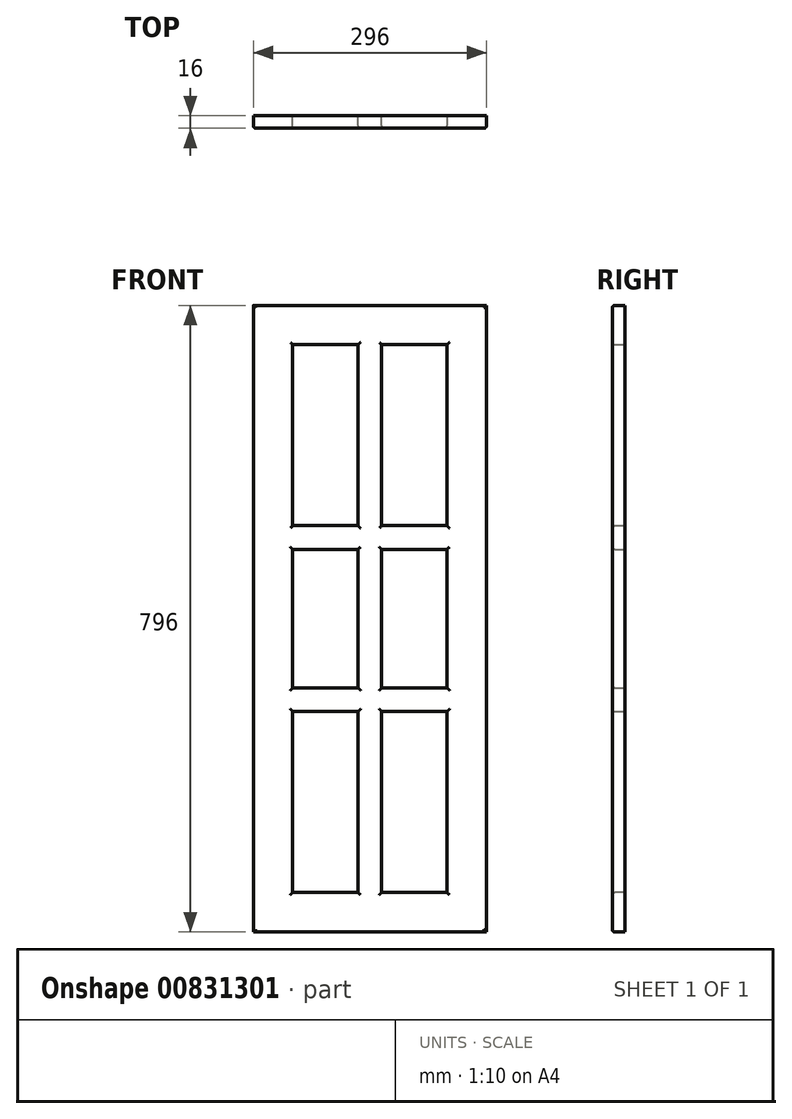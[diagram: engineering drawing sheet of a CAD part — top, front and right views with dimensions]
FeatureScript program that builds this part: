
annotation { "Feature Type Name" : "Feature", "Feature Type Description" : "" }
export const myFeature = defineFeature(function(context is Context, id is Id, definition is map)
    precondition{}
    {
        {
            var Q0;
            Q0=qCreatedBy(makeId("Front.planeOp"),FACE);
            var sketch = newSketch(context, id + "F0", { "sketchPlane" : qUnion([Q0])});
            skLineSegment(sketch, "E0.bottom", {"start": v(0, 0) * mm, "end": v(28.85, 0) * mm});
            skLineSegment(sketch, "E0.top", {"start": v(0, 37.88) * mm, "end": v(28.85, 37.88) * mm});
            skLineSegment(sketch, "E0.left", {"start": v(0, 0) * mm, "end": v(0, 37.88) * mm});
            skLineSegment(sketch, "E0.right", {"start": v(28.85, 0) * mm, "end": v(28.85, 37.88) * mm});
            skSolve(sketch);
        }
        {
            var Q0;
            Q0=makeQuery(id+"F0.imprint","IMPRINT",FACE,{"disambiguationData":[TD([[makeQuery(id+"F0.imprint","IMPRINT",EDGE,{"derivedFrom":sQuery(id+"F0.wireOp",EDGE,"E0.bottom")}),1.0]])]});
            extrude(context, id + "F1", {"entities" : qUnion([Q0]), "depth" : 16 * mm, "offsetDistance" : 25.4 * mm});
        }
        {
            var Q0;
            Q0=makeQuery(id+"F1.opExtrude","SWEPT_FACE",FACE,{"disambiguationData":[OSD([sQuery(id+"F0.wireOp",EDGE,"E0.left")])]});
            extrude(context, id + "F2", {"entities" : qUnion([Q0]), "operationType" : NewBodyOperationType.ADD, "oppositeDirection" : true, "depth" : 296 * mm, "offsetDistance" : 25.4 * mm});
        }
        {
            var Q0;
            {var subQ0=sQuery(id+"F0.wireOp",EDGE,"E0.bottom");Q0=makeQuery(id+"F2.boolean.opBoolean","MERGE",FACE,{"derivedFrom":[makeQuery(id+"F1.opExtrude","SWEPT_FACE",FACE,{"disambiguationData":[OSD([subQ0])]}),makeQuery(id+"F2.opExtrude","SWEPT_FACE",FACE,{"disambiguationData":[OSD([subQ0,sQuery(id+"F0.wireOp",EDGE,"E0.left")])]})]});}
            extrude(context, id + "F3", {"entities" : qUnion([Q0]), "operationType" : NewBodyOperationType.ADD, "oppositeDirection" : true, "depth" : 996 * mm, "offsetDistance" : 25 * mm});
        }
        {
            var Q0;
            {var subQ0=sQuery(id+"F0.wireOp",EDGE,"E0.left");var subQ1=sQuery(id+"F0.wireOp",EDGE,"E0.bottom");Q0=makeQuery(id+"F3.boolean.opBoolean","MERGE",FACE,{"derivedFrom":[makeQuery(id+"F2.boolean.opBoolean","MERGE",FACE,{"derivedFrom":[makeQuery(id+"F1.opExtrude","CAP_FACE",FACE,{"disambiguationData":[OSD([subQ1,sQuery(id+"F0.wireOp",EDGE,"E0.top"),subQ0,sQuery(id+"F0.wireOp",EDGE,"E0.right")])],"isStart":false}),makeQuery(id+"F2.opExtrude","SWEPT_FACE",FACE,{"disambiguationData":[OSD([subQ0]),TDD([makeQuery(id+"F1.opExtrude","CAP_EDGE",EDGE,{"disambiguationData":[OSD([subQ0])],"isStart":false})])]})]}),makeQuery(id+"F3.opExtrude","SWEPT_FACE",FACE,{"disambiguationData":[OSD([subQ1,subQ0]),TDD([makeQuery(id+"F2.boolean.opBoolean","MERGE",EDGE,{"derivedFrom":[makeQuery(id+"F1.opExtrude","CAP_EDGE",EDGE,{"disambiguationData":[OSD([subQ1])],"isStart":false}),makeQuery(id+"F2.opExtrude","SWEPT_EDGE",EDGE,{"disambiguationData":[OSD([subQ1,subQ0]),TDD([makeQuery(id+"F1.opExtrude","CAP_VERTEX",VERTEX,{"disambiguationData":[OSD([subQ1,subQ0])],"isStart":false})])]})]})])]})]});}
            var sketch = newSketch(context, id + "F4", { "sketchPlane" : qUnion([Q0])});
            skLineSegment(sketch, "E1.bottom", {"start": v(48.4, 906.79) * mm, "end": v(248.24, 906.79) * mm});
            skLineSegment(sketch, "E1.top", {"start": v(48.4, 105.66) * mm, "end": v(248.24, 105.66) * mm});
            skLineSegment(sketch, "E1.left", {"start": v(48.4, 906.79) * mm, "end": v(48.4, 105.66) * mm});
            skLineSegment(sketch, "E1.right", {"start": v(248.24, 906.79) * mm, "end": v(248.24, 105.66) * mm});
            skSolve(sketch);
        }
        {
            var Q0;
            Q0=makeQuery(id+"F4.imprint","IMPRINT",FACE,{"disambiguationData":[TD([[makeQuery(id+"F4.imprint","IMPRINT",EDGE,{"derivedFrom":sQuery(id+"F4.wireOp",EDGE,"E1.bottom")}),-1.0]])]});
            extrude(context, id + "F5", {"entities" : qUnion([Q0]), "operationType" : NewBodyOperationType.REMOVE, "oppositeDirection" : true, "depth" : 5 * mm, "offsetDistance" : 25 * mm});
        }
        {
            var Q0;
            Q0=makeQuery(id+"F5.boolean.opBoolean","COPY",FACE,{"derivedFrom":makeQuery(id+"F5.opExtrude","SWEPT_FACE",FACE,{"disambiguationData":[OSD([sQuery(id+"F4.wireOp",EDGE,"E1.bottom")])]})});
            extrude(context, id + "F6", {"entities" : qUnion([Q0]), "operationType" : NewBodyOperationType.REMOVE, "oppositeDirection" : true, "depth" : 39.2 * mm, "offsetDistance" : 25 * mm});
        }
        {
            var Q0;
            {var subQ0=sQuery(id+"F4.wireOp",EDGE,"E1.right");Q0=makeQuery(id+"F6.boolean.opBoolean","MERGE",FACE,{"derivedFrom":[makeQuery(id+"F5.boolean.opBoolean","COPY",FACE,{"derivedFrom":makeQuery(id+"F5.opExtrude","SWEPT_FACE",FACE,{"disambiguationData":[OSD([subQ0])]})}),makeQuery(id+"F6.opExtrude","SWEPT_FACE",FACE,{"disambiguationData":[OSD([sQuery(id+"F4.wireOp",EDGE,"E1.bottom"),subQ0])]})]});}
            extrude(context, id + "F7", {"entities" : qUnion([Q0]), "operationType" : NewBodyOperationType.ADD, "depth" : 2.24 * mm, "offsetDistance" : 25 * mm});
        }
        {
            var Q0;
            Q0=makeQuery(id+"F5.boolean.opBoolean","COPY",FACE,{"derivedFrom":makeQuery(id+"F5.opExtrude","SWEPT_FACE",FACE,{"disambiguationData":[OSD([sQuery(id+"F4.wireOp",EDGE,"E1.top")])]})});
            extrude(context, id + "F8", {"entities" : qUnion([Q0]), "operationType" : NewBodyOperationType.REMOVE, "oppositeDirection" : true, "depth" : 55.66 * mm, "offsetDistance" : 25 * mm});
        }
        {
            var Q0;
            {var subQ0=sQuery(id+"F4.wireOp",EDGE,"E1.left");Q0=makeQuery(id+"F8.boolean.opBoolean","MERGE",FACE,{"derivedFrom":[makeQuery(id+"F6.boolean.opBoolean","MERGE",FACE,{"derivedFrom":[makeQuery(id+"F5.boolean.opBoolean","COPY",FACE,{"derivedFrom":makeQuery(id+"F5.opExtrude","SWEPT_FACE",FACE,{"disambiguationData":[OSD([subQ0])]})}),makeQuery(id+"F6.opExtrude","SWEPT_FACE",FACE,{"disambiguationData":[OSD([sQuery(id+"F4.wireOp",EDGE,"E1.bottom"),subQ0])]})]}),makeQuery(id+"F8.opExtrude","SWEPT_FACE",FACE,{"disambiguationData":[OSD([sQuery(id+"F4.wireOp",EDGE,"E1.top"),subQ0])]})]});}
            extrude(context, id + "F9", {"entities" : qUnion([Q0]), "operationType" : NewBodyOperationType.ADD, "depth" : 1.59 * mm, "offsetDistance" : 25 * mm});
        }
        {
            var Q0;
            {var subQ0=sQuery(id+"F4.wireOp",EDGE,"E1.top");var subQ1=sQuery(id+"F4.wireOp",EDGE,"E1.bottom");Q0=makeQuery(id+"F8.boolean.opBoolean","MERGE",FACE,{"derivedFrom":[makeQuery(id+"F6.boolean.opBoolean","MERGE",FACE,{"derivedFrom":[makeQuery(id+"F5.boolean.opBoolean","COPY",FACE,{"derivedFrom":makeQuery(id+"F5.opExtrude","CAP_FACE",FACE,{"disambiguationData":[OSD([subQ1,subQ0,sQuery(id+"F4.wireOp",EDGE,"E1.left"),sQuery(id+"F4.wireOp",EDGE,"E1.right")])],"isStart":false})}),makeQuery(id+"F6.opExtrude","SWEPT_FACE",FACE,{"disambiguationData":[OSD([subQ1]),TDD([makeQuery(id+"F5.boolean.opBoolean","COPY",EDGE,{"derivedFrom":makeQuery(id+"F5.opExtrude","CAP_EDGE",EDGE,{"disambiguationData":[OSD([subQ1])],"isStart":false})})])]})]}),makeQuery(id+"F8.opExtrude","SWEPT_FACE",FACE,{"disambiguationData":[OSD([subQ0]),TDD([makeQuery(id+"F5.boolean.opBoolean","COPY",EDGE,{"derivedFrom":makeQuery(id+"F5.opExtrude","CAP_EDGE",EDGE,{"disambiguationData":[OSD([subQ0])],"isStart":false})})])]})]});}
            var sketch = newSketch(context, id + "F10", { "sketchPlane" : qUnion([Q0])});
            skLineSegment(sketch, "E2.bottom", {"start": v(127.14, 946) * mm, "end": v(181.91, 946) * mm});
            skLineSegment(sketch, "E2.top", {"start": v(127.14, 50) * mm, "end": v(181.91, 50) * mm});
            skLineSegment(sketch, "E2.left", {"start": v(127.14, 946) * mm, "end": v(127.14, 50) * mm});
            skLineSegment(sketch, "E2.right", {"start": v(181.91, 946) * mm, "end": v(181.91, 50) * mm});
            skSolve(sketch);
        }
        {
            var Q0;
            Q0=makeQuery(id+"F10.imprint","IMPRINT",FACE,{"disambiguationData":[TD([[makeQuery(id+"F10.imprint","IMPRINT",EDGE,{"derivedFrom":sQuery(id+"F10.wireOp",EDGE,"E2.bottom")}),-1.0]])]});
            extrude(context, id + "F11", {"entities" : qUnion([Q0]), "operationType" : NewBodyOperationType.ADD, "depth" : 5 * mm, "offsetDistance" : 25 * mm});
        }
        {
            var Q0;
            Q0=makeQuery(id+"F11.opExtrude","SWEPT_FACE",FACE,{"disambiguationData":[OSD([sQuery(id+"F10.wireOp",EDGE,"E2.left")])]});
            extrude(context, id + "F12", {"entities" : qUnion([Q0]), "operationType" : NewBodyOperationType.REMOVE, "oppositeDirection" : true, "depth" : 5.86 * mm, "offsetDistance" : 25 * mm});
        }
        {
            var Q0;
            Q0=makeQuery(id+"F11.opExtrude","SWEPT_FACE",FACE,{"disambiguationData":[OSD([sQuery(id+"F10.wireOp",EDGE,"E2.right")])]});
            extrude(context, id + "F13", {"entities" : qUnion([Q0]), "operationType" : NewBodyOperationType.REMOVE, "oppositeDirection" : true, "depth" : 18.91 * mm, "offsetDistance" : 25 * mm});
        }
        {
            var Q0;
            {var subQ0=sQuery(id+"F10.wireOp",EDGE,"E2.left");var subQ1=sQuery(id+"F4.wireOp",EDGE,"E1.bottom");var subQ2=sQuery(id+"F4.wireOp",EDGE,"E1.top");var subQ3=sQuery(id+"F4.wireOp",EDGE,"E1.left");Q0=makeQuery(id+"F12.boolean.opBoolean","MERGE",FACE,{"derivedFrom":[makeQuery(id+"F11.boolean.opBoolean","SPLIT",FACE,{"disambiguationData":[TD([makeQuery(id+"F11.opExtrude","SWEPT_FACE",FACE,{"disambiguationData":[OSD([subQ0])]})])],"derivedFrom":makeQuery(id+"F8.boolean.opBoolean","MERGE",FACE,{"derivedFrom":[makeQuery(id+"F6.boolean.opBoolean","MERGE",FACE,{"derivedFrom":[makeQuery(id+"F5.boolean.opBoolean","COPY",FACE,{"derivedFrom":makeQuery(id+"F5.opExtrude","CAP_FACE",FACE,{"disambiguationData":[OSD([subQ1,subQ2,subQ3,sQuery(id+"F4.wireOp",EDGE,"E1.right")])],"isStart":false})}),makeQuery(id+"F6.opExtrude","SWEPT_FACE",FACE,{"disambiguationData":[OSD([subQ1]),TDD([makeQuery(id+"F5.boolean.opBoolean","COPY",EDGE,{"derivedFrom":makeQuery(id+"F5.opExtrude","CAP_EDGE",EDGE,{"disambiguationData":[OSD([subQ1])],"isStart":false})})])]})]}),makeQuery(id+"F8.opExtrude","SWEPT_FACE",FACE,{"disambiguationData":[OSD([subQ2]),TDD([makeQuery(id+"F5.boolean.opBoolean","COPY",EDGE,{"derivedFrom":makeQuery(id+"F5.opExtrude","CAP_EDGE",EDGE,{"disambiguationData":[OSD([subQ2])],"isStart":false})})])]})]})}),makeQuery(id+"F12.opExtrude","SWEPT_FACE",FACE,{"disambiguationData":[OSD([subQ0]),TDD([makeQuery(id+"F11.opExtrude","CAP_EDGE",EDGE,{"disambiguationData":[OSD([subQ0])],"isStart":true})])]})]});}
            var sketch = newSketch(context, id + "F14", { "sketchPlane" : qUnion([Q0])});
            skLineSegment(sketch, "E3.bottom", {"start": v(50, 870.78) * mm, "end": v(133, 870.78) * mm});
            skLineSegment(sketch, "E3.top", {"start": v(50, 835.83) * mm, "end": v(133, 835.83) * mm});
            skLineSegment(sketch, "E3.left", {"start": v(50, 870.78) * mm, "end": v(50, 835.83) * mm});
            skLineSegment(sketch, "E3.right", {"start": v(133, 870.78) * mm, "end": v(133, 835.83) * mm});
            skLineSegment(sketch, "E4.bottom", {"start": v(50, 539.3) * mm, "end": v(133, 539.3) * mm});
            skLineSegment(sketch, "E4.top", {"start": v(50, 484.02) * mm, "end": v(133, 484.02) * mm});
            skLineSegment(sketch, "E4.left", {"start": v(50, 539.3) * mm, "end": v(50, 484.02) * mm});
            skLineSegment(sketch, "E4.right", {"start": v(133, 539.3) * mm, "end": v(133, 484.02) * mm});
            skSolve(sketch);
        }
        {
            var Q0;
            {var subQ0=sQuery(id+"F10.wireOp",EDGE,"E2.right");var subQ1=sQuery(id+"F4.wireOp",EDGE,"E1.top");var subQ2=sQuery(id+"F4.wireOp",EDGE,"E1.right");var subQ3=sQuery(id+"F4.wireOp",EDGE,"E1.bottom");Q0=makeQuery(id+"F13.boolean.opBoolean","MERGE",FACE,{"derivedFrom":[makeQuery(id+"F11.boolean.opBoolean","SPLIT",FACE,{"disambiguationData":[TD([makeQuery(id+"F11.opExtrude","SWEPT_FACE",FACE,{"disambiguationData":[OSD([subQ0])]})])],"derivedFrom":makeQuery(id+"F8.boolean.opBoolean","MERGE",FACE,{"derivedFrom":[makeQuery(id+"F6.boolean.opBoolean","MERGE",FACE,{"derivedFrom":[makeQuery(id+"F5.boolean.opBoolean","COPY",FACE,{"derivedFrom":makeQuery(id+"F5.opExtrude","CAP_FACE",FACE,{"disambiguationData":[OSD([subQ3,subQ1,sQuery(id+"F4.wireOp",EDGE,"E1.left"),subQ2])],"isStart":false})}),makeQuery(id+"F6.opExtrude","SWEPT_FACE",FACE,{"disambiguationData":[OSD([subQ3]),TDD([makeQuery(id+"F5.boolean.opBoolean","COPY",EDGE,{"derivedFrom":makeQuery(id+"F5.opExtrude","CAP_EDGE",EDGE,{"disambiguationData":[OSD([subQ3])],"isStart":false})})])]})]}),makeQuery(id+"F8.opExtrude","SWEPT_FACE",FACE,{"disambiguationData":[OSD([subQ1]),TDD([makeQuery(id+"F5.boolean.opBoolean","COPY",EDGE,{"derivedFrom":makeQuery(id+"F5.opExtrude","CAP_EDGE",EDGE,{"disambiguationData":[OSD([subQ1])],"isStart":false})})])]})]})}),makeQuery(id+"F13.opExtrude","SWEPT_FACE",FACE,{"disambiguationData":[OSD([subQ0]),TDD([makeQuery(id+"F11.opExtrude","CAP_EDGE",EDGE,{"disambiguationData":[OSD([subQ0])],"isStart":true})])]})]});}
            var sketch = newSketch(context, id + "F15", { "sketchPlane" : qUnion([Q0])});
            skLineSegment(sketch, "E5.bottom", {"start": v(163, 876.14) * mm, "end": v(246, 876.14) * mm});
            skLineSegment(sketch, "E5.top", {"start": v(163, 831.26) * mm, "end": v(246, 831.26) * mm});
            skLineSegment(sketch, "E5.left", {"start": v(163, 876.14) * mm, "end": v(163, 831.26) * mm});
            skLineSegment(sketch, "E5.right", {"start": v(246, 876.14) * mm, "end": v(246, 831.26) * mm});
            skLineSegment(sketch, "E6.bottom", {"start": v(163, 602.8) * mm, "end": v(246, 602.8) * mm});
            skLineSegment(sketch, "E6.top", {"start": v(163, 550.28) * mm, "end": v(246, 550.28) * mm});
            skLineSegment(sketch, "E6.left", {"start": v(163, 602.8) * mm, "end": v(163, 550.28) * mm});
            skLineSegment(sketch, "E6.right", {"start": v(246, 602.8) * mm, "end": v(246, 550.28) * mm});
            skSolve(sketch);
        }
        {
            var Q0;
            Q0=makeQuery(id+"F14.imprint","IMPRINT",FACE,{"disambiguationData":[TD([[makeQuery(id+"F14.imprint","IMPRINT",EDGE,{"derivedFrom":sQuery(id+"F14.wireOp",EDGE,"E3.bottom")}),-1.0]])]});
            var Q1;
            Q1=makeQuery(id+"F15.imprint","IMPRINT",FACE,{"disambiguationData":[TD([[makeQuery(id+"F15.imprint","IMPRINT",EDGE,{"derivedFrom":sQuery(id+"F15.wireOp",EDGE,"E5.bottom")}),-1.0]])]});
            var Q2;
            Q2=makeQuery(id+"F15.imprint","IMPRINT",FACE,{"disambiguationData":[TD([[makeQuery(id+"F15.imprint","IMPRINT",EDGE,{"derivedFrom":sQuery(id+"F15.wireOp",EDGE,"E6.bottom")}),-1.0]])]});
            var Q3;
            Q3=makeQuery(id+"F14.imprint","IMPRINT",FACE,{"disambiguationData":[TD([[makeQuery(id+"F14.imprint","IMPRINT",EDGE,{"derivedFrom":sQuery(id+"F14.wireOp",EDGE,"E4.bottom")}),-1.0]])]});
            extrude(context, id + "F16", {"entities" : qUnion([Q0, Q1, Q2, Q3]), "operationType" : NewBodyOperationType.ADD, "depth" : 5 * mm, "offsetDistance" : 25 * mm});
        }
        {
            var Q0;
            Q0=makeQuery(id+"F16.opExtrude","SWEPT_FACE",FACE,{"disambiguationData":[OSD([sQuery(id+"F15.wireOp",EDGE,"E6.top")])]});
            var Q1;
            Q1=makeQuery(id+"F16.opExtrude","SWEPT_FACE",FACE,{"disambiguationData":[OSD([sQuery(id+"F14.wireOp",EDGE,"E4.top")])]});
            extrude(context, id + "F17", {"entities" : qUnion([Q0, Q1]), "operationType" : NewBodyOperationType.ADD, "depth" : 300 * mm, "offsetDistance" : 25 * mm});
        }
        {
            var Q0;
            Q0=makeQuery(id+"F16.opExtrude","SWEPT_FACE",FACE,{"disambiguationData":[OSD([sQuery(id+"F14.wireOp",EDGE,"E4.bottom")])]});
            var Q1;
            Q1=makeQuery(id+"F16.opExtrude","SWEPT_FACE",FACE,{"disambiguationData":[OSD([sQuery(id+"F15.wireOp",EDGE,"E6.bottom")])]});
            extrude(context, id + "F18", {"entities" : qUnion([Q0, Q1]), "operationType" : NewBodyOperationType.REMOVE, "oppositeDirection" : true, "depth" : 300 * mm, "offsetDistance" : 25 * mm});
        }
        {
            var Q0;
            Q0=makeQuery(id+"F16.opExtrude","SWEPT_FACE",FACE,{"disambiguationData":[OSD([sQuery(id+"F14.wireOp",EDGE,"E3.top")])]});
            extrude(context, id + "F19", {"entities" : qUnion([Q0]), "operationType" : NewBodyOperationType.ADD, "depth" : 324.8 * mm, "offsetDistance" : 25 * mm});
        }
        {
            var Q0;
            Q0=makeQuery(id+"F16.opExtrude","SWEPT_FACE",FACE,{"disambiguationData":[OSD([sQuery(id+"F14.wireOp",EDGE,"E3.bottom")])]});
            extrude(context, id + "F20", {"entities" : qUnion([Q0]), "operationType" : NewBodyOperationType.REMOVE, "oppositeDirection" : true, "depth" : 324.8 * mm, "offsetDistance" : 25 * mm});
        }
        {
            var Q0;
            Q0=makeQuery(id+"F18.boolean.opBoolean","COPY",FACE,{"derivedFrom":makeQuery(id+"F18.opExtrude","CAP_FACE",FACE,{"disambiguationData":[OSD([sQuery(id+"F14.wireOp",EDGE,"E4.bottom")])],"isStart":false})});
            extrude(context, id + "F21", {"entities" : qUnion([Q0]), "operationType" : NewBodyOperationType.ADD, "depth" : 250 * mm, "offsetDistance" : 25 * mm});
        }
        {
            var Q0;
            Q0=makeQuery(id+"F17.opExtrude","CAP_FACE",FACE,{"disambiguationData":[OSD([sQuery(id+"F14.wireOp",EDGE,"E4.top")])],"isStart":false});
            extrude(context, id + "F22", {"entities" : qUnion([Q0]), "operationType" : NewBodyOperationType.REMOVE, "oppositeDirection" : true, "depth" : 250 * mm, "offsetDistance" : 25 * mm});
        }
        {
            var Q0;
            Q0=makeQuery(id+"F20.boolean.opBoolean","COPY",FACE,{"derivedFrom":makeQuery(id+"F20.opExtrude","CAP_FACE",FACE,{"disambiguationData":[OSD([sQuery(id+"F14.wireOp",EDGE,"E3.bottom")])],"isStart":false})});
            extrude(context, id + "F23", {"entities" : qUnion([Q0]), "operationType" : NewBodyOperationType.ADD, "depth" : 100 * mm, "offsetDistance" : 25 * mm});
        }
        {
            var Q0;
            Q0=makeQuery(id+"F19.opExtrude","CAP_FACE",FACE,{"disambiguationData":[OSD([sQuery(id+"F14.wireOp",EDGE,"E3.top")])],"isStart":false});
            extrude(context, id + "F24", {"entities" : qUnion([Q0]), "operationType" : NewBodyOperationType.REMOVE, "oppositeDirection" : true, "depth" : 100 * mm, "offsetDistance" : 25 * mm});
        }
        {
            var Q0;
            Q0=makeQuery(id+"F23.opExtrude","CAP_FACE",FACE,{"disambiguationData":[OSD([sQuery(id+"F14.wireOp",EDGE,"E3.bottom")])],"isStart":false});
            extrude(context, id + "F25", {"entities" : qUnion([Q0]), "operationType" : NewBodyOperationType.ADD, "depth" : 50 * mm, "offsetDistance" : 25 * mm});
        }
        {
            var Q0;
            Q0=makeQuery(id+"F24.boolean.opBoolean","COPY",FACE,{"derivedFrom":makeQuery(id+"F24.opExtrude","CAP_FACE",FACE,{"disambiguationData":[OSD([sQuery(id+"F14.wireOp",EDGE,"E3.top")])],"isStart":false})});
            extrude(context, id + "F26", {"entities" : qUnion([Q0]), "operationType" : NewBodyOperationType.REMOVE, "oppositeDirection" : true, "depth" : 50 * mm, "offsetDistance" : 25 * mm});
        }
        {
            var Q0;
            Q0=makeQuery(id+"F22.boolean.opBoolean","COPY",FACE,{"derivedFrom":makeQuery(id+"F22.opExtrude","CAP_FACE",FACE,{"disambiguationData":[OSD([sQuery(id+"F14.wireOp",EDGE,"E4.top")])],"isStart":false})});
            extrude(context, id + "F27", {"entities" : qUnion([Q0]), "operationType" : NewBodyOperationType.ADD, "depth" : 134.02 * mm, "offsetDistance" : 25 * mm});
        }
        {
            var Q0;
            Q0=makeQuery(id+"F27.opExtrude","CAP_FACE",FACE,{"disambiguationData":[OSD([sQuery(id+"F14.wireOp",EDGE,"E4.top")])],"isStart":false});
            extrude(context, id + "F28", {"entities" : qUnion([Q0]), "operationType" : NewBodyOperationType.REMOVE, "oppositeDirection" : true, "depth" : 100 * mm, "offsetDistance" : 25 * mm});
        }
        {
            var Q0;
            Q0=makeQuery(id+"F26.boolean.opBoolean","COPY",FACE,{"derivedFrom":makeQuery(id+"F26.opExtrude","CAP_FACE",FACE,{"disambiguationData":[OSD([sQuery(id+"F14.wireOp",EDGE,"E3.top")])],"isStart":false})});
            extrude(context, id + "F29", {"entities" : qUnion([Q0]), "operationType" : NewBodyOperationType.ADD, "depth" : 100 * mm, "offsetDistance" : 25 * mm});
        }
        {
            var Q0;
            Q0=makeQuery(id+"F25.opExtrude","CAP_FACE",FACE,{"disambiguationData":[OSD([sQuery(id+"F14.wireOp",EDGE,"E3.bottom")])],"isStart":false});
            extrude(context, id + "F30", {"entities" : qUnion([Q0]), "operationType" : NewBodyOperationType.REMOVE, "oppositeDirection" : true, "depth" : 100 * mm, "offsetDistance" : 25 * mm});
        }
        {
            var Q0;
            Q0=makeQuery(id+"F30.boolean.opBoolean","COPY",FACE,{"derivedFrom":makeQuery(id+"F30.opExtrude","CAP_FACE",FACE,{"disambiguationData":[OSD([sQuery(id+"F14.wireOp",EDGE,"E3.bottom")])],"isStart":false})});
            extrude(context, id + "F31", {"entities" : qUnion([Q0]), "operationType" : NewBodyOperationType.ADD, "depth" : 50 * mm, "offsetDistance" : 25 * mm});
        }
        {
            var Q0;
            Q0=makeQuery(id+"F29.opExtrude","CAP_FACE",FACE,{"disambiguationData":[OSD([sQuery(id+"F14.wireOp",EDGE,"E3.top")])],"isStart":false});
            extrude(context, id + "F32", {"entities" : qUnion([Q0]), "operationType" : NewBodyOperationType.REMOVE, "oppositeDirection" : true, "depth" : 54.95 * mm, "offsetDistance" : 25 * mm});
        }
        {
            var Q0;
            Q0=makeQuery(id+"F28.boolean.opBoolean","COPY",FACE,{"derivedFrom":makeQuery(id+"F28.opExtrude","CAP_FACE",FACE,{"disambiguationData":[OSD([sQuery(id+"F14.wireOp",EDGE,"E4.top")])],"isStart":false})});
            extrude(context, id + "F33", {"entities" : qUnion([Q0]), "operationType" : NewBodyOperationType.ADD, "depth" : 50 * mm, "offsetDistance" : 25 * mm});
        }
        {
            var Q0;
            Q0=makeQuery(id+"F21.opExtrude","CAP_FACE",FACE,{"disambiguationData":[OSD([sQuery(id+"F14.wireOp",EDGE,"E4.bottom")])],"isStart":false});
            extrude(context, id + "F34", {"entities" : qUnion([Q0]), "operationType" : NewBodyOperationType.REMOVE, "oppositeDirection" : true, "depth" : 109.3 * mm, "offsetDistance" : 25 * mm});
        }
        {
            var Q0;
            Q0=makeQuery(id+"F16.opExtrude","SWEPT_FACE",FACE,{"disambiguationData":[OSD([sQuery(id+"F15.wireOp",EDGE,"E5.top")])]});
            extrude(context, id + "F35", {"entities" : qUnion([Q0]), "operationType" : NewBodyOperationType.REMOVE, "oppositeDirection" : true, "depth" : 14.88 * mm, "offsetDistance" : 25 * mm});
        }
        {
            var Q0;
            Q0=makeQuery(id+"F35.boolean.opBoolean","COPY",FACE,{"derivedFrom":makeQuery(id+"F35.opExtrude","CAP_FACE",FACE,{"disambiguationData":[OSD([sQuery(id+"F15.wireOp",EDGE,"E5.top")])],"isStart":false})});
            extrude(context, id + "F36", {"entities" : qUnion([Q0]), "operationType" : NewBodyOperationType.ADD, "depth" : 230.15 * mm, "offsetDistance" : 25 * mm});
        }
        {
            var Q0;
            Q0=makeQuery(id+"F16.opExtrude","SWEPT_FACE",FACE,{"disambiguationData":[OSD([sQuery(id+"F15.wireOp",EDGE,"E5.bottom")])]});
            extrude(context, id + "F37", {"entities" : qUnion([Q0]), "operationType" : NewBodyOperationType.REMOVE, "oppositeDirection" : true, "depth" : 230.15 * mm, "offsetDistance" : 25 * mm});
        }
        {
            var Q0;
            Q0=makeQuery(id+"F17.opExtrude","CAP_FACE",FACE,{"disambiguationData":[OSD([sQuery(id+"F15.wireOp",EDGE,"E6.top")])],"isStart":false});
            extrude(context, id + "F38", {"entities" : qUnion([Q0]), "operationType" : NewBodyOperationType.REMOVE, "oppositeDirection" : true, "depth" : 22.52 * mm, "offsetDistance" : 25 * mm});
        }
        {
            var Q0;
            Q0=makeQuery(id+"F18.boolean.opBoolean","COPY",FACE,{"derivedFrom":makeQuery(id+"F18.opExtrude","CAP_FACE",FACE,{"disambiguationData":[OSD([sQuery(id+"F15.wireOp",EDGE,"E6.bottom")])],"isStart":false})});
            extrude(context, id + "F39", {"entities" : qUnion([Q0]), "operationType" : NewBodyOperationType.ADD, "depth" : 77.2 * mm, "offsetDistance" : 25 * mm});
        }
        {
            var Q0;
            Q0=makeQuery(id+"F38.boolean.opBoolean","COPY",FACE,{"derivedFrom":makeQuery(id+"F38.opExtrude","CAP_FACE",FACE,{"disambiguationData":[OSD([sQuery(id+"F15.wireOp",EDGE,"E6.top")])],"isStart":false})});
            extrude(context, id + "F40", {"entities" : qUnion([Q0]), "operationType" : NewBodyOperationType.REMOVE, "oppositeDirection" : true, "depth" : 77.2 * mm, "offsetDistance" : 25 * mm});
        }
        {
            var Q0;
            {var subQ0=sQuery(id+"F14.wireOp",EDGE,"E3.bottom");var subQ1=makeQuery(id+"F16.opExtrude","CAP_EDGE",EDGE,{"disambiguationData":[OSD([subQ0])],"isStart":true});var subQ2=sQuery(id+"F10.wireOp",EDGE,"E2.left");var subQ3=sQuery(id+"F4.wireOp",EDGE,"E1.bottom");var subQ4=sQuery(id+"F4.wireOp",EDGE,"E1.left");var subQ5=sQuery(id+"F4.wireOp",EDGE,"E1.top");var subQ7=makeQuery(id+"F6.boolean.opBoolean","COPY",FACE,{"derivedFrom":makeQuery(id+"F6.opExtrude","CAP_FACE",FACE,{"disambiguationData":[OSD([subQ3])],"isStart":false})});Q0=makeQuery(id+"F30.boolean.opBoolean","MERGE",FACE,{"derivedFrom":[makeQuery(id+"F20.boolean.opBoolean","MERGE",FACE,{"derivedFrom":[makeQuery(id+"F16.boolean.opBoolean","SPLIT",FACE,{"disambiguationData":[TD([subQ7])],"derivedFrom":makeQuery(id+"F12.boolean.opBoolean","MERGE",FACE,{"derivedFrom":[makeQuery(id+"F11.boolean.opBoolean","SPLIT",FACE,{"disambiguationData":[TD([makeQuery(id+"F11.opExtrude","SWEPT_FACE",FACE,{"disambiguationData":[OSD([subQ2])]})])],"derivedFrom":makeQuery(id+"F8.boolean.opBoolean","MERGE",FACE,{"derivedFrom":[makeQuery(id+"F6.boolean.opBoolean","MERGE",FACE,{"derivedFrom":[makeQuery(id+"F5.boolean.opBoolean","COPY",FACE,{"derivedFrom":makeQuery(id+"F5.opExtrude","CAP_FACE",FACE,{"disambiguationData":[OSD([subQ3,subQ5,subQ4,sQuery(id+"F4.wireOp",EDGE,"E1.right")])],"isStart":false})}),makeQuery(id+"F6.opExtrude","SWEPT_FACE",FACE,{"disambiguationData":[OSD([subQ3]),TDD([makeQuery(id+"F5.boolean.opBoolean","COPY",EDGE,{"derivedFrom":makeQuery(id+"F5.opExtrude","CAP_EDGE",EDGE,{"disambiguationData":[OSD([subQ3])],"isStart":false})})])]})]}),makeQuery(id+"F8.opExtrude","SWEPT_FACE",FACE,{"disambiguationData":[OSD([subQ5]),TDD([makeQuery(id+"F5.boolean.opBoolean","COPY",EDGE,{"derivedFrom":makeQuery(id+"F5.opExtrude","CAP_EDGE",EDGE,{"disambiguationData":[OSD([subQ5])],"isStart":false})})])]})]})}),makeQuery(id+"F12.opExtrude","SWEPT_FACE",FACE,{"disambiguationData":[OSD([subQ2]),TDD([makeQuery(id+"F11.opExtrude","CAP_EDGE",EDGE,{"disambiguationData":[OSD([subQ2])],"isStart":true})])]})]})}),makeQuery(id+"F20.opExtrude","SWEPT_FACE",FACE,{"disambiguationData":[OSD([subQ0]),TDD([subQ1])]})]}),makeQuery(id+"F30.opExtrude","SWEPT_FACE",FACE,{"disambiguationData":[OSD([subQ0]),TDD([makeQuery(id+"F25.opExtrude","CAP_EDGE",EDGE,{"disambiguationData":[OSD([subQ0]),TDD([makeQuery(id+"F23.opExtrude","CAP_EDGE",EDGE,{"disambiguationData":[OSD([subQ0]),TDD([makeQuery(id+"F20.boolean.opBoolean","COPY",EDGE,{"derivedFrom":makeQuery(id+"F20.opExtrude","CAP_EDGE",EDGE,{"disambiguationData":[OSD([subQ0]),TDD([subQ1])],"isStart":false})})])],"isStart":false})])],"isStart":false})])]})]});}
            var Q1;
            {var subQ0=sQuery(id+"F15.wireOp",EDGE,"E5.bottom");var subQ1=sQuery(id+"F10.wireOp",EDGE,"E2.right");var subQ2=sQuery(id+"F4.wireOp",EDGE,"E1.bottom");var subQ3=sQuery(id+"F4.wireOp",EDGE,"E1.right");var subQ4=sQuery(id+"F4.wireOp",EDGE,"E1.top");var subQ7=makeQuery(id+"F6.boolean.opBoolean","COPY",FACE,{"derivedFrom":makeQuery(id+"F6.opExtrude","CAP_FACE",FACE,{"disambiguationData":[OSD([subQ2])],"isStart":false})});Q1=makeQuery(id+"F37.boolean.opBoolean","MERGE",FACE,{"derivedFrom":[makeQuery(id+"F16.boolean.opBoolean","SPLIT",FACE,{"disambiguationData":[TD([subQ7])],"derivedFrom":makeQuery(id+"F13.boolean.opBoolean","MERGE",FACE,{"derivedFrom":[makeQuery(id+"F11.boolean.opBoolean","SPLIT",FACE,{"disambiguationData":[TD([makeQuery(id+"F11.opExtrude","SWEPT_FACE",FACE,{"disambiguationData":[OSD([subQ1])]})])],"derivedFrom":makeQuery(id+"F8.boolean.opBoolean","MERGE",FACE,{"derivedFrom":[makeQuery(id+"F6.boolean.opBoolean","MERGE",FACE,{"derivedFrom":[makeQuery(id+"F5.boolean.opBoolean","COPY",FACE,{"derivedFrom":makeQuery(id+"F5.opExtrude","CAP_FACE",FACE,{"disambiguationData":[OSD([subQ2,subQ4,sQuery(id+"F4.wireOp",EDGE,"E1.left"),subQ3])],"isStart":false})}),makeQuery(id+"F6.opExtrude","SWEPT_FACE",FACE,{"disambiguationData":[OSD([subQ2]),TDD([makeQuery(id+"F5.boolean.opBoolean","COPY",EDGE,{"derivedFrom":makeQuery(id+"F5.opExtrude","CAP_EDGE",EDGE,{"disambiguationData":[OSD([subQ2])],"isStart":false})})])]})]}),makeQuery(id+"F8.opExtrude","SWEPT_FACE",FACE,{"disambiguationData":[OSD([subQ4]),TDD([makeQuery(id+"F5.boolean.opBoolean","COPY",EDGE,{"derivedFrom":makeQuery(id+"F5.opExtrude","CAP_EDGE",EDGE,{"disambiguationData":[OSD([subQ4])],"isStart":false})})])]})]})}),makeQuery(id+"F13.opExtrude","SWEPT_FACE",FACE,{"disambiguationData":[OSD([subQ1]),TDD([makeQuery(id+"F11.opExtrude","CAP_EDGE",EDGE,{"disambiguationData":[OSD([subQ1])],"isStart":true})])]})]})}),makeQuery(id+"F37.opExtrude","SWEPT_FACE",FACE,{"disambiguationData":[OSD([subQ0]),TDD([makeQuery(id+"F16.opExtrude","CAP_EDGE",EDGE,{"disambiguationData":[OSD([subQ0])],"isStart":true})])]})]});}
            var Q2;
            {var subQ0=sQuery(id+"F15.wireOp",EDGE,"E5.top");var subQ1=sQuery(id+"F15.wireOp",EDGE,"E6.bottom");var subQ2=sQuery(id+"F10.wireOp",EDGE,"E2.right");var subQ3=sQuery(id+"F4.wireOp",EDGE,"E1.right");var subQ4=sQuery(id+"F4.wireOp",EDGE,"E1.top");var subQ6=sQuery(id+"F4.wireOp",EDGE,"E1.bottom");Q2=makeQuery(id+"F35.boolean.opBoolean","MERGE",FACE,{"derivedFrom":[makeQuery(id+"F18.boolean.opBoolean","MERGE",FACE,{"derivedFrom":[makeQuery(id+"F16.boolean.opBoolean","SPLIT",FACE,{"disambiguationData":[TD([makeQuery(id+"F16.opExtrude","SWEPT_FACE",FACE,{"disambiguationData":[OSD([subQ0])]})])],"derivedFrom":makeQuery(id+"F13.boolean.opBoolean","MERGE",FACE,{"derivedFrom":[makeQuery(id+"F11.boolean.opBoolean","SPLIT",FACE,{"disambiguationData":[TD([makeQuery(id+"F11.opExtrude","SWEPT_FACE",FACE,{"disambiguationData":[OSD([subQ2])]})])],"derivedFrom":makeQuery(id+"F8.boolean.opBoolean","MERGE",FACE,{"derivedFrom":[makeQuery(id+"F6.boolean.opBoolean","MERGE",FACE,{"derivedFrom":[makeQuery(id+"F5.boolean.opBoolean","COPY",FACE,{"derivedFrom":makeQuery(id+"F5.opExtrude","CAP_FACE",FACE,{"disambiguationData":[OSD([subQ6,subQ4,sQuery(id+"F4.wireOp",EDGE,"E1.left"),subQ3])],"isStart":false})}),makeQuery(id+"F6.opExtrude","SWEPT_FACE",FACE,{"disambiguationData":[OSD([subQ6]),TDD([makeQuery(id+"F5.boolean.opBoolean","COPY",EDGE,{"derivedFrom":makeQuery(id+"F5.opExtrude","CAP_EDGE",EDGE,{"disambiguationData":[OSD([subQ6])],"isStart":false})})])]})]}),makeQuery(id+"F8.opExtrude","SWEPT_FACE",FACE,{"disambiguationData":[OSD([subQ4]),TDD([makeQuery(id+"F5.boolean.opBoolean","COPY",EDGE,{"derivedFrom":makeQuery(id+"F5.opExtrude","CAP_EDGE",EDGE,{"disambiguationData":[OSD([subQ4])],"isStart":false})})])]})]})}),makeQuery(id+"F13.opExtrude","SWEPT_FACE",FACE,{"disambiguationData":[OSD([subQ2]),TDD([makeQuery(id+"F11.opExtrude","CAP_EDGE",EDGE,{"disambiguationData":[OSD([subQ2])],"isStart":true})])]})]})}),makeQuery(id+"F18.opExtrude","SWEPT_FACE",FACE,{"disambiguationData":[OSD([subQ1]),TDD([makeQuery(id+"F16.opExtrude","CAP_EDGE",EDGE,{"disambiguationData":[OSD([subQ1])],"isStart":true})])]})]}),makeQuery(id+"F35.opExtrude","SWEPT_FACE",FACE,{"disambiguationData":[OSD([subQ0]),TDD([makeQuery(id+"F16.opExtrude","CAP_EDGE",EDGE,{"disambiguationData":[OSD([subQ0])],"isStart":true})])]})]});}
            var Q3;
            {var subQ0=sQuery(id+"F14.wireOp",EDGE,"E4.bottom");var subQ1=makeQuery(id+"F16.opExtrude","CAP_EDGE",EDGE,{"disambiguationData":[OSD([subQ0])],"isStart":true});var subQ2=sQuery(id+"F14.wireOp",EDGE,"E3.top");var subQ3=makeQuery(id+"F19.opExtrude","CAP_EDGE",EDGE,{"disambiguationData":[OSD([subQ2]),TDD([makeQuery(id+"F16.opExtrude","CAP_EDGE",EDGE,{"disambiguationData":[OSD([subQ2])],"isStart":true})])],"isStart":false});var subQ4=makeQuery(id+"F24.boolean.opBoolean","COPY",EDGE,{"derivedFrom":makeQuery(id+"F24.opExtrude","CAP_EDGE",EDGE,{"disambiguationData":[OSD([subQ2]),TDD([subQ3])],"isStart":false})});var subQ5=sQuery(id+"F4.wireOp",EDGE,"E1.left");var subQ6=sQuery(id+"F4.wireOp",EDGE,"E1.top");var subQ7=sQuery(id+"F4.wireOp",EDGE,"E1.bottom");var subQ9=sQuery(id+"F10.wireOp",EDGE,"E2.left");Q3=makeQuery(id+"F34.boolean.opBoolean","MERGE",FACE,{"derivedFrom":[makeQuery(id+"F32.boolean.opBoolean","MERGE",FACE,{"derivedFrom":[makeQuery(id+"F26.boolean.opBoolean","MERGE",FACE,{"derivedFrom":[makeQuery(id+"F24.boolean.opBoolean","MERGE",FACE,{"derivedFrom":[makeQuery(id+"F18.boolean.opBoolean","MERGE",FACE,{"derivedFrom":[makeQuery(id+"F16.boolean.opBoolean","SPLIT",FACE,{"disambiguationData":[TD([makeQuery(id+"F16.opExtrude","SWEPT_FACE",FACE,{"disambiguationData":[OSD([subQ2])]})])],"derivedFrom":makeQuery(id+"F12.boolean.opBoolean","MERGE",FACE,{"derivedFrom":[makeQuery(id+"F11.boolean.opBoolean","SPLIT",FACE,{"disambiguationData":[TD([makeQuery(id+"F11.opExtrude","SWEPT_FACE",FACE,{"disambiguationData":[OSD([subQ9])]})])],"derivedFrom":makeQuery(id+"F8.boolean.opBoolean","MERGE",FACE,{"derivedFrom":[makeQuery(id+"F6.boolean.opBoolean","MERGE",FACE,{"derivedFrom":[makeQuery(id+"F5.boolean.opBoolean","COPY",FACE,{"derivedFrom":makeQuery(id+"F5.opExtrude","CAP_FACE",FACE,{"disambiguationData":[OSD([subQ7,subQ6,subQ5,sQuery(id+"F4.wireOp",EDGE,"E1.right")])],"isStart":false})}),makeQuery(id+"F6.opExtrude","SWEPT_FACE",FACE,{"disambiguationData":[OSD([subQ7]),TDD([makeQuery(id+"F5.boolean.opBoolean","COPY",EDGE,{"derivedFrom":makeQuery(id+"F5.opExtrude","CAP_EDGE",EDGE,{"disambiguationData":[OSD([subQ7])],"isStart":false})})])]})]}),makeQuery(id+"F8.opExtrude","SWEPT_FACE",FACE,{"disambiguationData":[OSD([subQ6]),TDD([makeQuery(id+"F5.boolean.opBoolean","COPY",EDGE,{"derivedFrom":makeQuery(id+"F5.opExtrude","CAP_EDGE",EDGE,{"disambiguationData":[OSD([subQ6])],"isStart":false})})])]})]})}),makeQuery(id+"F12.opExtrude","SWEPT_FACE",FACE,{"disambiguationData":[OSD([subQ9]),TDD([makeQuery(id+"F11.opExtrude","CAP_EDGE",EDGE,{"disambiguationData":[OSD([subQ9])],"isStart":true})])]})]})}),makeQuery(id+"F18.opExtrude","SWEPT_FACE",FACE,{"disambiguationData":[OSD([subQ0]),TDD([subQ1])]})]}),makeQuery(id+"F24.opExtrude","SWEPT_FACE",FACE,{"disambiguationData":[OSD([subQ2]),TDD([subQ3])]})]}),makeQuery(id+"F26.opExtrude","SWEPT_FACE",FACE,{"disambiguationData":[OSD([subQ2]),TDD([subQ4])]})]}),makeQuery(id+"F32.opExtrude","SWEPT_FACE",FACE,{"disambiguationData":[OSD([subQ2]),TDD([makeQuery(id+"F29.opExtrude","CAP_EDGE",EDGE,{"disambiguationData":[OSD([subQ2]),TDD([makeQuery(id+"F26.boolean.opBoolean","COPY",EDGE,{"derivedFrom":makeQuery(id+"F26.opExtrude","CAP_EDGE",EDGE,{"disambiguationData":[OSD([subQ2]),TDD([subQ4])],"isStart":false})})])],"isStart":false})])]})]}),makeQuery(id+"F34.opExtrude","SWEPT_FACE",FACE,{"disambiguationData":[OSD([subQ0]),TDD([makeQuery(id+"F21.opExtrude","CAP_EDGE",EDGE,{"disambiguationData":[OSD([subQ0]),TDD([makeQuery(id+"F18.boolean.opBoolean","COPY",EDGE,{"derivedFrom":makeQuery(id+"F18.opExtrude","CAP_EDGE",EDGE,{"disambiguationData":[OSD([subQ0]),TDD([subQ1])],"isStart":false})})])],"isStart":false})])]})]});}
            var Q4;
            {var subQ0=sQuery(id+"F14.wireOp",EDGE,"E4.top");var subQ1=makeQuery(id+"F17.opExtrude","CAP_EDGE",EDGE,{"disambiguationData":[OSD([subQ0]),TDD([makeQuery(id+"F16.opExtrude","CAP_EDGE",EDGE,{"disambiguationData":[OSD([subQ0])],"isStart":true})])],"isStart":false});var subQ2=sQuery(id+"F10.wireOp",EDGE,"E2.left");var subQ3=sQuery(id+"F4.wireOp",EDGE,"E1.top");var subQ4=sQuery(id+"F4.wireOp",EDGE,"E1.left");var subQ5=sQuery(id+"F4.wireOp",EDGE,"E1.bottom");var subQ7=makeQuery(id+"F8.boolean.opBoolean","COPY",FACE,{"derivedFrom":makeQuery(id+"F8.opExtrude","CAP_FACE",FACE,{"disambiguationData":[OSD([subQ3])],"isStart":false})});Q4=makeQuery(id+"F28.boolean.opBoolean","MERGE",FACE,{"derivedFrom":[makeQuery(id+"F22.boolean.opBoolean","MERGE",FACE,{"derivedFrom":[makeQuery(id+"F16.boolean.opBoolean","SPLIT",FACE,{"disambiguationData":[TD([subQ7])],"derivedFrom":makeQuery(id+"F12.boolean.opBoolean","MERGE",FACE,{"derivedFrom":[makeQuery(id+"F11.boolean.opBoolean","SPLIT",FACE,{"disambiguationData":[TD([makeQuery(id+"F11.opExtrude","SWEPT_FACE",FACE,{"disambiguationData":[OSD([subQ2])]})])],"derivedFrom":makeQuery(id+"F8.boolean.opBoolean","MERGE",FACE,{"derivedFrom":[makeQuery(id+"F6.boolean.opBoolean","MERGE",FACE,{"derivedFrom":[makeQuery(id+"F5.boolean.opBoolean","COPY",FACE,{"derivedFrom":makeQuery(id+"F5.opExtrude","CAP_FACE",FACE,{"disambiguationData":[OSD([subQ5,subQ3,subQ4,sQuery(id+"F4.wireOp",EDGE,"E1.right")])],"isStart":false})}),makeQuery(id+"F6.opExtrude","SWEPT_FACE",FACE,{"disambiguationData":[OSD([subQ5]),TDD([makeQuery(id+"F5.boolean.opBoolean","COPY",EDGE,{"derivedFrom":makeQuery(id+"F5.opExtrude","CAP_EDGE",EDGE,{"disambiguationData":[OSD([subQ5])],"isStart":false})})])]})]}),makeQuery(id+"F8.opExtrude","SWEPT_FACE",FACE,{"disambiguationData":[OSD([subQ3]),TDD([makeQuery(id+"F5.boolean.opBoolean","COPY",EDGE,{"derivedFrom":makeQuery(id+"F5.opExtrude","CAP_EDGE",EDGE,{"disambiguationData":[OSD([subQ3])],"isStart":false})})])]})]})}),makeQuery(id+"F12.opExtrude","SWEPT_FACE",FACE,{"disambiguationData":[OSD([subQ2]),TDD([makeQuery(id+"F11.opExtrude","CAP_EDGE",EDGE,{"disambiguationData":[OSD([subQ2])],"isStart":true})])]})]})}),makeQuery(id+"F22.opExtrude","SWEPT_FACE",FACE,{"disambiguationData":[OSD([subQ0]),TDD([subQ1])]})]}),makeQuery(id+"F28.opExtrude","SWEPT_FACE",FACE,{"disambiguationData":[OSD([subQ0]),TDD([makeQuery(id+"F27.opExtrude","CAP_EDGE",EDGE,{"disambiguationData":[OSD([subQ0]),TDD([makeQuery(id+"F22.boolean.opBoolean","COPY",EDGE,{"derivedFrom":makeQuery(id+"F22.opExtrude","CAP_EDGE",EDGE,{"disambiguationData":[OSD([subQ0]),TDD([subQ1])],"isStart":false})})])],"isStart":false})])]})]});}
            var Q5;
            {var subQ0=sQuery(id+"F15.wireOp",EDGE,"E6.top");var subQ1=makeQuery(id+"F17.opExtrude","CAP_EDGE",EDGE,{"disambiguationData":[OSD([subQ0]),TDD([makeQuery(id+"F16.opExtrude","CAP_EDGE",EDGE,{"disambiguationData":[OSD([subQ0])],"isStart":true})])],"isStart":false});var subQ2=sQuery(id+"F10.wireOp",EDGE,"E2.right");var subQ3=sQuery(id+"F4.wireOp",EDGE,"E1.top");var subQ4=makeQuery(id+"F8.boolean.opBoolean","COPY",FACE,{"derivedFrom":makeQuery(id+"F8.opExtrude","CAP_FACE",FACE,{"disambiguationData":[OSD([subQ3])],"isStart":false})});var subQ5=sQuery(id+"F4.wireOp",EDGE,"E1.right");var subQ7=sQuery(id+"F4.wireOp",EDGE,"E1.bottom");Q5=makeQuery(id+"F40.boolean.opBoolean","MERGE",FACE,{"derivedFrom":[makeQuery(id+"F38.boolean.opBoolean","MERGE",FACE,{"derivedFrom":[makeQuery(id+"F16.boolean.opBoolean","SPLIT",FACE,{"disambiguationData":[TD([subQ4])],"derivedFrom":makeQuery(id+"F13.boolean.opBoolean","MERGE",FACE,{"derivedFrom":[makeQuery(id+"F11.boolean.opBoolean","SPLIT",FACE,{"disambiguationData":[TD([makeQuery(id+"F11.opExtrude","SWEPT_FACE",FACE,{"disambiguationData":[OSD([subQ2])]})])],"derivedFrom":makeQuery(id+"F8.boolean.opBoolean","MERGE",FACE,{"derivedFrom":[makeQuery(id+"F6.boolean.opBoolean","MERGE",FACE,{"derivedFrom":[makeQuery(id+"F5.boolean.opBoolean","COPY",FACE,{"derivedFrom":makeQuery(id+"F5.opExtrude","CAP_FACE",FACE,{"disambiguationData":[OSD([subQ7,subQ3,sQuery(id+"F4.wireOp",EDGE,"E1.left"),subQ5])],"isStart":false})}),makeQuery(id+"F6.opExtrude","SWEPT_FACE",FACE,{"disambiguationData":[OSD([subQ7]),TDD([makeQuery(id+"F5.boolean.opBoolean","COPY",EDGE,{"derivedFrom":makeQuery(id+"F5.opExtrude","CAP_EDGE",EDGE,{"disambiguationData":[OSD([subQ7])],"isStart":false})})])]})]}),makeQuery(id+"F8.opExtrude","SWEPT_FACE",FACE,{"disambiguationData":[OSD([subQ3]),TDD([makeQuery(id+"F5.boolean.opBoolean","COPY",EDGE,{"derivedFrom":makeQuery(id+"F5.opExtrude","CAP_EDGE",EDGE,{"disambiguationData":[OSD([subQ3])],"isStart":false})})])]})]})}),makeQuery(id+"F13.opExtrude","SWEPT_FACE",FACE,{"disambiguationData":[OSD([subQ2]),TDD([makeQuery(id+"F11.opExtrude","CAP_EDGE",EDGE,{"disambiguationData":[OSD([subQ2])],"isStart":true})])]})]})}),makeQuery(id+"F38.opExtrude","SWEPT_FACE",FACE,{"disambiguationData":[OSD([subQ0]),TDD([subQ1])]})]}),makeQuery(id+"F40.opExtrude","SWEPT_FACE",FACE,{"disambiguationData":[OSD([subQ0]),TDD([makeQuery(id+"F38.boolean.opBoolean","COPY",EDGE,{"derivedFrom":makeQuery(id+"F38.opExtrude","CAP_EDGE",EDGE,{"disambiguationData":[OSD([subQ0]),TDD([subQ1])],"isStart":false})})])]})]});}
            extrude(context, id + "F41", {"entities" : qUnion([Q0, Q1, Q2, Q3, Q4, Q5]), "operationType" : NewBodyOperationType.REMOVE, "oppositeDirection" : true, "depth" : 11 * mm, "offsetDistance" : 25 * mm});
        }
        {
            var Q0;
            {var subQ0=sQuery(id+"F15.wireOp",EDGE,"E5.top");Q0=makeQuery(id+"F41.boolean.opBoolean","MERGE",FACE,{"derivedFrom":[makeQuery(id+"F36.opExtrude","CAP_FACE",FACE,{"disambiguationData":[OSD([subQ0])],"isStart":false}),makeQuery(id+"F41.opExtrude","SWEPT_FACE",FACE,{"disambiguationData":[OSD([subQ0])]})]});}
            var Q1;
            {var subQ0=sQuery(id+"F14.wireOp",EDGE,"E3.top");Q1=makeQuery(id+"F41.boolean.opBoolean","MERGE",FACE,{"derivedFrom":[makeQuery(id+"F32.boolean.opBoolean","COPY",FACE,{"derivedFrom":makeQuery(id+"F32.opExtrude","CAP_FACE",FACE,{"disambiguationData":[OSD([subQ0])],"isStart":false})}),makeQuery(id+"F41.opExtrude","SWEPT_FACE",FACE,{"disambiguationData":[OSD([subQ0])]})]});}
            extrude(context, id + "F42", {"entities" : qUnion([Q0, Q1]), "operationType" : NewBodyOperationType.ADD, "depth" : 200 * mm, "offsetDistance" : 25 * mm});
        }
        {
            var Q0;
            {var subQ0=sQuery(id+"F10.wireOp",EDGE,"E2.left");var subQ1=sQuery(id+"F10.wireOp",EDGE,"E2.bottom");var subQ2=sQuery(id+"F4.wireOp",EDGE,"E1.bottom");Q0=makeQuery(id+"F41.boolean.opBoolean","MERGE",FACE,{"derivedFrom":[makeQuery(id+"F12.boolean.opBoolean","MERGE",FACE,{"derivedFrom":[makeQuery(id+"F11.boolean.opBoolean","SPLIT",FACE,{"disambiguationData":[TD([makeQuery(id+"F11.opExtrude","SWEPT_FACE",FACE,{"disambiguationData":[OSD([subQ0])]})])],"derivedFrom":makeQuery(id+"F6.boolean.opBoolean","COPY",FACE,{"derivedFrom":makeQuery(id+"F6.opExtrude","CAP_FACE",FACE,{"disambiguationData":[OSD([subQ2])],"isStart":false})})}),makeQuery(id+"F12.opExtrude","SWEPT_FACE",FACE,{"disambiguationData":[OSD([subQ2,subQ1,subQ0])]})]}),makeQuery(id+"F41.opExtrude","SWEPT_FACE",FACE,{"disambiguationData":[OSD([subQ2,subQ1,subQ0])]})]});}
            var Q1;
            {var subQ0=sQuery(id+"F10.wireOp",EDGE,"E2.right");var subQ1=sQuery(id+"F10.wireOp",EDGE,"E2.bottom");var subQ2=sQuery(id+"F4.wireOp",EDGE,"E1.bottom");Q1=makeQuery(id+"F41.boolean.opBoolean","MERGE",FACE,{"derivedFrom":[makeQuery(id+"F13.boolean.opBoolean","MERGE",FACE,{"derivedFrom":[makeQuery(id+"F11.boolean.opBoolean","SPLIT",FACE,{"disambiguationData":[TD([makeQuery(id+"F11.opExtrude","SWEPT_FACE",FACE,{"disambiguationData":[OSD([subQ0])]})])],"derivedFrom":makeQuery(id+"F6.boolean.opBoolean","COPY",FACE,{"derivedFrom":makeQuery(id+"F6.opExtrude","CAP_FACE",FACE,{"disambiguationData":[OSD([subQ2])],"isStart":false})})}),makeQuery(id+"F13.opExtrude","SWEPT_FACE",FACE,{"disambiguationData":[OSD([subQ2,subQ1,subQ0])]})]}),makeQuery(id+"F41.opExtrude","SWEPT_FACE",FACE,{"disambiguationData":[OSD([subQ2,subQ1,subQ0])]})]});}
            extrude(context, id + "F43", {"entities" : qUnion([Q0, Q1]), "operationType" : NewBodyOperationType.ADD, "depth" : 200 * mm, "offsetDistance" : 25 * mm});
        }
        {
            var Q0;
            Q0=makeQuery(id+"F3.opExtrude","CAP_FACE",FACE,{"disambiguationData":[OSD([sQuery(id+"F0.wireOp",EDGE,"E0.bottom"),sQuery(id+"F0.wireOp",EDGE,"E0.left")])],"isStart":false});
            var Q1;
            {var subQ0=sQuery(id+"F14.wireOp",EDGE,"E3.bottom");Q1=makeQuery(id+"F41.boolean.opBoolean","MERGE",FACE,{"derivedFrom":[makeQuery(id+"F31.opExtrude","CAP_FACE",FACE,{"disambiguationData":[OSD([subQ0])],"isStart":false}),makeQuery(id+"F41.opExtrude","SWEPT_FACE",FACE,{"disambiguationData":[OSD([subQ0])]})]});}
            var Q2;
            {var subQ0=sQuery(id+"F15.wireOp",EDGE,"E5.bottom");Q2=makeQuery(id+"F41.boolean.opBoolean","MERGE",FACE,{"derivedFrom":[makeQuery(id+"F37.boolean.opBoolean","COPY",FACE,{"derivedFrom":makeQuery(id+"F37.opExtrude","CAP_FACE",FACE,{"disambiguationData":[OSD([subQ0])],"isStart":false})}),makeQuery(id+"F41.opExtrude","SWEPT_FACE",FACE,{"disambiguationData":[OSD([subQ0])]})]});}
            extrude(context, id + "F44", {"entities" : qUnion([Q0, Q1, Q2]), "operationType" : NewBodyOperationType.REMOVE, "oppositeDirection" : true, "depth" : 200 * mm, "offsetDistance" : 25 * mm});
        }
        {
            var Q0;
            {var subQ0=sQuery(id+"F15.wireOp",EDGE,"E6.top");Q0=makeQuery(id+"F41.boolean.opBoolean","MERGE",FACE,{"derivedFrom":[makeQuery(id+"F40.boolean.opBoolean","COPY",FACE,{"derivedFrom":makeQuery(id+"F40.opExtrude","CAP_FACE",FACE,{"disambiguationData":[OSD([subQ0])],"isStart":false})}),makeQuery(id+"F41.opExtrude","SWEPT_FACE",FACE,{"disambiguationData":[OSD([subQ0])]})]});}
            var Q1;
            {var subQ0=sQuery(id+"F14.wireOp",EDGE,"E4.top");Q1=makeQuery(id+"F41.boolean.opBoolean","MERGE",FACE,{"derivedFrom":[makeQuery(id+"F33.opExtrude","CAP_FACE",FACE,{"disambiguationData":[OSD([subQ0])],"isStart":false}),makeQuery(id+"F41.opExtrude","SWEPT_FACE",FACE,{"disambiguationData":[OSD([subQ0])]})]});}
            extrude(context, id + "F45", {"entities" : qUnion([Q0, Q1]), "operationType" : NewBodyOperationType.ADD, "depth" : 70 * mm, "offsetDistance" : 25 * mm});
        }
        {
            var Q0;
            {var subQ0=sQuery(id+"F15.wireOp",EDGE,"E6.bottom");Q0=makeQuery(id+"F41.boolean.opBoolean","MERGE",FACE,{"derivedFrom":[makeQuery(id+"F39.opExtrude","CAP_FACE",FACE,{"disambiguationData":[OSD([subQ0])],"isStart":false}),makeQuery(id+"F41.opExtrude","SWEPT_FACE",FACE,{"disambiguationData":[OSD([subQ0])]})]});}
            var Q1;
            {var subQ0=sQuery(id+"F14.wireOp",EDGE,"E4.bottom");Q1=makeQuery(id+"F41.boolean.opBoolean","MERGE",FACE,{"derivedFrom":[makeQuery(id+"F34.boolean.opBoolean","COPY",FACE,{"derivedFrom":makeQuery(id+"F34.opExtrude","CAP_FACE",FACE,{"disambiguationData":[OSD([subQ0])],"isStart":false})}),makeQuery(id+"F41.opExtrude","SWEPT_FACE",FACE,{"disambiguationData":[OSD([subQ0])]})]});}
            extrude(context, id + "F46", {"entities" : qUnion([Q0, Q1]), "operationType" : NewBodyOperationType.REMOVE, "oppositeDirection" : true, "depth" : 70 * mm, "offsetDistance" : 25 * mm});
        }
        {
            var Q0;
            Q0=makeQuery(id+"F44.boolean.opBoolean","COPY",FACE,{"derivedFrom":makeQuery(id+"F44.opExtrude","CAP_FACE",FACE,{"disambiguationData":[OSD([sQuery(id+"F15.wireOp",EDGE,"E5.bottom")])],"isStart":false})});
            var Q1;
            Q1=makeQuery(id+"F44.boolean.opBoolean","COPY",FACE,{"derivedFrom":makeQuery(id+"F44.opExtrude","CAP_FACE",FACE,{"disambiguationData":[OSD([sQuery(id+"F14.wireOp",EDGE,"E3.bottom")])],"isStart":false})});
            extrude(context, id + "F47", {"entities" : qUnion([Q0, Q1]), "operationType" : NewBodyOperationType.ADD, "depth" : 70 * mm, "offsetDistance" : 25 * mm});
        }
        {
            var Q0;
            Q0=makeQuery(id+"F42.opExtrude","CAP_FACE",FACE,{"disambiguationData":[OSD([sQuery(id+"F15.wireOp",EDGE,"E5.top")])],"isStart":false});
            var Q1;
            Q1=makeQuery(id+"F42.opExtrude","CAP_FACE",FACE,{"disambiguationData":[OSD([sQuery(id+"F14.wireOp",EDGE,"E3.top")])],"isStart":false});
            extrude(context, id + "F48", {"entities" : qUnion([Q0, Q1]), "operationType" : NewBodyOperationType.REMOVE, "oppositeDirection" : true, "depth" : 70 * mm, "offsetDistance" : 25 * mm});
        }
        {
            var Q0;
            {var subQ0=sQuery(id+"F15.wireOp",EDGE,"E5.bottom");var subQ1=sQuery(id+"F14.wireOp",EDGE,"E3.bottom");var subQ2=makeQuery(id+"F20.boolean.opBoolean","COPY",EDGE,{"derivedFrom":makeQuery(id+"F20.opExtrude","CAP_EDGE",EDGE,{"disambiguationData":[OSD([subQ1]),TDD([makeQuery(id+"F16.opExtrude","CAP_EDGE",EDGE,{"disambiguationData":[OSD([subQ1])],"isStart":false})])],"isStart":false})});var subQ3=makeQuery(id+"F23.opExtrude","CAP_EDGE",EDGE,{"disambiguationData":[OSD([subQ1]),TDD([subQ2])],"isStart":false});var subQ4=makeQuery(id+"F30.boolean.opBoolean","COPY",EDGE,{"derivedFrom":makeQuery(id+"F30.opExtrude","CAP_EDGE",EDGE,{"disambiguationData":[OSD([subQ1]),TDD([makeQuery(id+"F25.opExtrude","CAP_EDGE",EDGE,{"disambiguationData":[OSD([subQ1]),TDD([subQ3])],"isStart":false})])],"isStart":false})});var subQ5=sQuery(id+"F15.wireOp",EDGE,"E6.top");var subQ6=makeQuery(id+"F16.opExtrude","CAP_EDGE",EDGE,{"disambiguationData":[OSD([subQ5])],"isStart":false});var subQ7=sQuery(id+"F14.wireOp",EDGE,"E4.top");var subQ8=makeQuery(id+"F16.opExtrude","CAP_EDGE",EDGE,{"disambiguationData":[OSD([subQ7])],"isStart":false});var subQ9=makeQuery(id+"F22.boolean.opBoolean","COPY",EDGE,{"derivedFrom":makeQuery(id+"F22.opExtrude","CAP_EDGE",EDGE,{"disambiguationData":[OSD([subQ7]),TDD([makeQuery(id+"F17.opExtrude","CAP_EDGE",EDGE,{"disambiguationData":[OSD([subQ7]),TDD([subQ8])],"isStart":false})])],"isStart":false})});var subQ10=makeQuery(id+"F28.boolean.opBoolean","COPY",EDGE,{"derivedFrom":makeQuery(id+"F28.opExtrude","CAP_EDGE",EDGE,{"disambiguationData":[OSD([subQ7]),TDD([makeQuery(id+"F27.opExtrude","CAP_EDGE",EDGE,{"disambiguationData":[OSD([subQ7]),TDD([subQ9])],"isStart":false})])],"isStart":false})});var subQ11=sQuery(id+"F10.wireOp",EDGE,"E2.right");var subQ12=sQuery(id+"F10.wireOp",EDGE,"E2.bottom");var subQ13=sQuery(id+"F4.wireOp",EDGE,"E1.bottom");var subQ15=sQuery(id+"F0.wireOp",EDGE,"E0.left");var subQ16=sQuery(id+"F0.wireOp",EDGE,"E0.bottom");var subQ17=makeQuery(id+"F3.opExtrude","SWEPT_FACE",FACE,{"disambiguationData":[OSD([subQ16,subQ15]),TDD([makeQuery(id+"F2.boolean.opBoolean","MERGE",EDGE,{"derivedFrom":[makeQuery(id+"F1.opExtrude","CAP_EDGE",EDGE,{"disambiguationData":[OSD([subQ16])],"isStart":false}),makeQuery(id+"F2.opExtrude","SWEPT_EDGE",EDGE,{"disambiguationData":[OSD([subQ16,subQ15]),TDD([makeQuery(id+"F1.opExtrude","CAP_VERTEX",VERTEX,{"disambiguationData":[OSD([subQ16,subQ15])],"isStart":false})])]})]})])]});var subQ18=makeQuery(id+"F2.opExtrude","SWEPT_FACE",FACE,{"disambiguationData":[OSD([subQ15]),TDD([makeQuery(id+"F1.opExtrude","CAP_EDGE",EDGE,{"disambiguationData":[OSD([subQ15])],"isStart":false})])]});var subQ19=makeQuery(id+"F1.opExtrude","CAP_FACE",FACE,{"disambiguationData":[OSD([subQ16,sQuery(id+"F0.wireOp",EDGE,"E0.top"),subQ15,sQuery(id+"F0.wireOp",EDGE,"E0.right")])],"isStart":false});var subQ20=sQuery(id+"F4.wireOp",EDGE,"E1.right");var subQ21=makeQuery(id+"F7.opExtrude","SWEPT_FACE",FACE,{"disambiguationData":[OSD([subQ13,subQ20]),TDD([makeQuery(id+"F6.boolean.opBoolean","MERGE",EDGE,{"derivedFrom":[makeQuery(id+"F5.boolean.opBoolean","COPY",EDGE,{"derivedFrom":makeQuery(id+"F5.opExtrude","CAP_EDGE",EDGE,{"disambiguationData":[OSD([subQ20])],"isStart":true})}),makeQuery(id+"F6.opExtrude","SWEPT_EDGE",EDGE,{"disambiguationData":[OSD([subQ13,subQ20]),TDD([makeQuery(id+"F5.boolean.opBoolean","COPY",VERTEX,{"derivedFrom":makeQuery(id+"F5.opExtrude","CAP_VERTEX",VERTEX,{"disambiguationData":[OSD([subQ13,subQ20])],"isStart":true})})])]})]})])]});var subQ22=sQuery(id+"F10.wireOp",EDGE,"E2.left");var subQ23=makeQuery(id+"F11.opExtrude","CAP_FACE",FACE,{"disambiguationData":[OSD([subQ12,sQuery(id+"F10.wireOp",EDGE,"E2.top"),subQ22,subQ11])],"isStart":false});var subQ24=sQuery(id+"F4.wireOp",EDGE,"E1.top");var subQ25=sQuery(id+"F4.wireOp",EDGE,"E1.left");var subQ26=makeQuery(id+"F9.opExtrude","SWEPT_FACE",FACE,{"disambiguationData":[OSD([subQ13,subQ24,subQ25]),TDD([makeQuery(id+"F8.boolean.opBoolean","MERGE",EDGE,{"derivedFrom":[makeQuery(id+"F6.boolean.opBoolean","MERGE",EDGE,{"derivedFrom":[makeQuery(id+"F5.boolean.opBoolean","COPY",EDGE,{"derivedFrom":makeQuery(id+"F5.opExtrude","CAP_EDGE",EDGE,{"disambiguationData":[OSD([subQ25])],"isStart":true})}),makeQuery(id+"F6.opExtrude","SWEPT_EDGE",EDGE,{"disambiguationData":[OSD([subQ13,subQ25]),TDD([makeQuery(id+"F5.boolean.opBoolean","COPY",VERTEX,{"derivedFrom":makeQuery(id+"F5.opExtrude","CAP_VERTEX",VERTEX,{"disambiguationData":[OSD([subQ13,subQ25])],"isStart":true})})])]})]}),makeQuery(id+"F8.opExtrude","SWEPT_EDGE",EDGE,{"disambiguationData":[OSD([subQ24,subQ25]),TDD([makeQuery(id+"F5.boolean.opBoolean","COPY",VERTEX,{"derivedFrom":makeQuery(id+"F5.opExtrude","CAP_VERTEX",VERTEX,{"disambiguationData":[OSD([subQ24,subQ25])],"isStart":true})})])]})]})])]});var subQ27=makeQuery(id+"F6.boolean.opBoolean","COPY",EDGE,{"derivedFrom":makeQuery(id+"F6.opExtrude","CAP_EDGE",EDGE,{"disambiguationData":[OSD([subQ13]),TDD([makeQuery(id+"F5.boolean.opBoolean","COPY",EDGE,{"derivedFrom":makeQuery(id+"F5.opExtrude","CAP_EDGE",EDGE,{"disambiguationData":[OSD([subQ13])],"isStart":true})})])],"isStart":false})});var subQ28=sQuery(id+"F15.wireOp",EDGE,"E5.top");var subQ29=makeQuery(id+"F35.boolean.opBoolean","COPY",EDGE,{"derivedFrom":makeQuery(id+"F35.opExtrude","CAP_EDGE",EDGE,{"disambiguationData":[OSD([subQ28]),TDD([makeQuery(id+"F16.opExtrude","CAP_EDGE",EDGE,{"disambiguationData":[OSD([subQ28])],"isStart":false})])],"isStart":false})});var subQ30=sQuery(id+"F14.wireOp",EDGE,"E3.top");var subQ31=makeQuery(id+"F16.opExtrude","CAP_EDGE",EDGE,{"disambiguationData":[OSD([subQ30])],"isStart":false});var subQ32=makeQuery(id+"F26.boolean.opBoolean","COPY",EDGE,{"derivedFrom":makeQuery(id+"F26.opExtrude","CAP_EDGE",EDGE,{"disambiguationData":[OSD([subQ30]),TDD([makeQuery(id+"F24.boolean.opBoolean","COPY",EDGE,{"derivedFrom":makeQuery(id+"F24.opExtrude","CAP_EDGE",EDGE,{"disambiguationData":[OSD([subQ30]),TDD([makeQuery(id+"F19.opExtrude","CAP_EDGE",EDGE,{"disambiguationData":[OSD([subQ30]),TDD([subQ31])],"isStart":false})])],"isStart":false})})])],"isStart":false})});var subQ33=sQuery(id+"F15.wireOp",EDGE,"E6.bottom");var subQ34=sQuery(id+"F14.wireOp",EDGE,"E4.bottom");Q0=makeQuery(id+"F47.boolean.opBoolean","MERGE",FACE,{"derivedFrom":[makeQuery(id+"F45.boolean.opBoolean","MERGE",FACE,{"derivedFrom":[makeQuery(id+"F43.boolean.opBoolean","MERGE",FACE,{"derivedFrom":[makeQuery(id+"F42.boolean.opBoolean","MERGE",FACE,{"derivedFrom":[makeQuery(id+"F39.boolean.opBoolean","MERGE",FACE,{"derivedFrom":[makeQuery(id+"F36.boolean.opBoolean","MERGE",FACE,{"derivedFrom":[makeQuery(id+"F33.boolean.opBoolean","MERGE",FACE,{"derivedFrom":[makeQuery(id+"F31.boolean.opBoolean","MERGE",FACE,{"derivedFrom":[makeQuery(id+"F29.boolean.opBoolean","MERGE",FACE,{"derivedFrom":[makeQuery(id+"F27.boolean.opBoolean","MERGE",FACE,{"derivedFrom":[makeQuery(id+"F25.boolean.opBoolean","MERGE",FACE,{"derivedFrom":[makeQuery(id+"F23.boolean.opBoolean","MERGE",FACE,{"derivedFrom":[makeQuery(id+"F21.boolean.opBoolean","MERGE",FACE,{"derivedFrom":[makeQuery(id+"F19.boolean.opBoolean","MERGE",FACE,{"derivedFrom":[makeQuery(id+"F17.boolean.opBoolean","MERGE",FACE,{"derivedFrom":[makeQuery(id+"F16.boolean.opBoolean","MERGE",FACE,{"derivedFrom":[makeQuery(id+"F11.boolean.opBoolean","MERGE",FACE,{"derivedFrom":[makeQuery(id+"F9.boolean.opBoolean","MERGE",FACE,{"derivedFrom":[makeQuery(id+"F7.boolean.opBoolean","MERGE",FACE,{"derivedFrom":[makeQuery(id+"F3.boolean.opBoolean","MERGE",FACE,{"derivedFrom":[makeQuery(id+"F2.boolean.opBoolean","MERGE",FACE,{"derivedFrom":[subQ19,subQ18]}),subQ17]}),subQ21]}),subQ26]}),subQ23]}),makeQuery(id+"F16.opExtrude","CAP_FACE",FACE,{"disambiguationData":[OSD([subQ1,subQ30,sQuery(id+"F14.wireOp",EDGE,"E3.left"),sQuery(id+"F14.wireOp",EDGE,"E3.right")])],"isStart":false}),makeQuery(id+"F16.opExtrude","CAP_FACE",FACE,{"disambiguationData":[OSD([subQ34,subQ7,sQuery(id+"F14.wireOp",EDGE,"E4.left"),sQuery(id+"F14.wireOp",EDGE,"E4.right")])],"isStart":false}),makeQuery(id+"F16.opExtrude","CAP_FACE",FACE,{"disambiguationData":[OSD([subQ0,subQ28,sQuery(id+"F15.wireOp",EDGE,"E5.left"),sQuery(id+"F15.wireOp",EDGE,"E5.right")])],"isStart":false}),makeQuery(id+"F16.opExtrude","CAP_FACE",FACE,{"disambiguationData":[OSD([subQ33,subQ5,sQuery(id+"F15.wireOp",EDGE,"E6.left"),sQuery(id+"F15.wireOp",EDGE,"E6.right")])],"isStart":false})]}),makeQuery(id+"F17.opExtrude","SWEPT_FACE",FACE,{"disambiguationData":[OSD([subQ7]),TDD([subQ8])]}),makeQuery(id+"F17.opExtrude","SWEPT_FACE",FACE,{"disambiguationData":[OSD([subQ5]),TDD([subQ6])]})]}),makeQuery(id+"F19.opExtrude","SWEPT_FACE",FACE,{"disambiguationData":[OSD([subQ30]),TDD([subQ31])]})]}),makeQuery(id+"F21.opExtrude","SWEPT_FACE",FACE,{"disambiguationData":[OSD([subQ34]),TDD([makeQuery(id+"F18.boolean.opBoolean","COPY",EDGE,{"derivedFrom":makeQuery(id+"F18.opExtrude","CAP_EDGE",EDGE,{"disambiguationData":[OSD([subQ34]),TDD([makeQuery(id+"F16.opExtrude","CAP_EDGE",EDGE,{"disambiguationData":[OSD([subQ34])],"isStart":false})])],"isStart":false})})])]})]}),makeQuery(id+"F23.opExtrude","SWEPT_FACE",FACE,{"disambiguationData":[OSD([subQ1]),TDD([subQ2])]})]}),makeQuery(id+"F25.opExtrude","SWEPT_FACE",FACE,{"disambiguationData":[OSD([subQ1]),TDD([subQ3])]})]}),makeQuery(id+"F27.opExtrude","SWEPT_FACE",FACE,{"disambiguationData":[OSD([subQ7]),TDD([subQ9])]})]}),makeQuery(id+"F29.opExtrude","SWEPT_FACE",FACE,{"disambiguationData":[OSD([subQ30]),TDD([subQ32])]})]}),makeQuery(id+"F31.opExtrude","SWEPT_FACE",FACE,{"disambiguationData":[OSD([subQ1]),TDD([subQ4])]})]}),makeQuery(id+"F33.opExtrude","SWEPT_FACE",FACE,{"disambiguationData":[OSD([subQ7]),TDD([subQ10])]})]}),makeQuery(id+"F36.opExtrude","SWEPT_FACE",FACE,{"disambiguationData":[OSD([subQ28]),TDD([subQ29])]})]}),makeQuery(id+"F39.opExtrude","SWEPT_FACE",FACE,{"disambiguationData":[OSD([subQ33]),TDD([makeQuery(id+"F18.boolean.opBoolean","COPY",EDGE,{"derivedFrom":makeQuery(id+"F18.opExtrude","CAP_EDGE",EDGE,{"disambiguationData":[OSD([subQ33]),TDD([makeQuery(id+"F16.opExtrude","CAP_EDGE",EDGE,{"disambiguationData":[OSD([subQ33])],"isStart":false})])],"isStart":false})})])]})]}),makeQuery(id+"F42.opExtrude","SWEPT_FACE",FACE,{"disambiguationData":[OSD([subQ30]),TDD([makeQuery(id+"F32.boolean.opBoolean","COPY",EDGE,{"derivedFrom":makeQuery(id+"F32.opExtrude","CAP_EDGE",EDGE,{"disambiguationData":[OSD([subQ30]),TDD([makeQuery(id+"F29.opExtrude","CAP_EDGE",EDGE,{"disambiguationData":[OSD([subQ30]),TDD([subQ32])],"isStart":false})])],"isStart":false})})])]}),makeQuery(id+"F42.opExtrude","SWEPT_FACE",FACE,{"disambiguationData":[OSD([subQ28]),TDD([makeQuery(id+"F36.opExtrude","CAP_EDGE",EDGE,{"disambiguationData":[OSD([subQ28]),TDD([subQ29])],"isStart":false})])]})]}),makeQuery(id+"F43.opExtrude","SWEPT_FACE",FACE,{"disambiguationData":[OSD([subQ13,subQ12,subQ22]),TDD([makeQuery(id+"F12.boolean.opBoolean","MERGE",EDGE,{"derivedFrom":[makeQuery(id+"F11.boolean.opBoolean","SPLIT",EDGE,{"disambiguationData":[TD([makeQuery(id+"F11.opExtrude","SWEPT_FACE",FACE,{"disambiguationData":[OSD([subQ22])]})])],"derivedFrom":subQ27}),makeQuery(id+"F12.opExtrude","SWEPT_EDGE",EDGE,{"disambiguationData":[OSD([subQ13,subQ12,subQ22]),TDD([makeQuery(id+"F11.opExtrude","CAP_VERTEX",VERTEX,{"disambiguationData":[OSD([subQ13,subQ12,subQ22])],"isStart":false})])]})]})])]}),makeQuery(id+"F43.opExtrude","SWEPT_FACE",FACE,{"disambiguationData":[OSD([subQ13,subQ12,subQ11]),TDD([makeQuery(id+"F13.boolean.opBoolean","MERGE",EDGE,{"derivedFrom":[makeQuery(id+"F11.boolean.opBoolean","SPLIT",EDGE,{"disambiguationData":[TD([makeQuery(id+"F11.opExtrude","SWEPT_FACE",FACE,{"disambiguationData":[OSD([subQ11])]})])],"derivedFrom":subQ27}),makeQuery(id+"F13.opExtrude","SWEPT_EDGE",EDGE,{"disambiguationData":[OSD([subQ13,subQ12,subQ11]),TDD([makeQuery(id+"F11.opExtrude","CAP_VERTEX",VERTEX,{"disambiguationData":[OSD([subQ13,subQ12,subQ11])],"isStart":false})])]})]})])]})]}),makeQuery(id+"F45.opExtrude","SWEPT_FACE",FACE,{"disambiguationData":[OSD([subQ7]),TDD([makeQuery(id+"F33.opExtrude","CAP_EDGE",EDGE,{"disambiguationData":[OSD([subQ7]),TDD([subQ10])],"isStart":false})])]}),makeQuery(id+"F45.opExtrude","SWEPT_FACE",FACE,{"disambiguationData":[OSD([subQ5]),TDD([makeQuery(id+"F40.boolean.opBoolean","COPY",EDGE,{"derivedFrom":makeQuery(id+"F40.opExtrude","CAP_EDGE",EDGE,{"disambiguationData":[OSD([subQ5]),TDD([makeQuery(id+"F38.boolean.opBoolean","COPY",EDGE,{"derivedFrom":makeQuery(id+"F38.opExtrude","CAP_EDGE",EDGE,{"disambiguationData":[OSD([subQ5]),TDD([makeQuery(id+"F17.opExtrude","CAP_EDGE",EDGE,{"disambiguationData":[OSD([subQ5]),TDD([subQ6])],"isStart":false})])],"isStart":false})})])],"isStart":false})})])]})]}),makeQuery(id+"F47.opExtrude","SWEPT_FACE",FACE,{"disambiguationData":[OSD([subQ1]),TDD([makeQuery(id+"F44.boolean.opBoolean","COPY",EDGE,{"derivedFrom":makeQuery(id+"F44.opExtrude","CAP_EDGE",EDGE,{"disambiguationData":[OSD([subQ1]),TDD([makeQuery(id+"F31.opExtrude","CAP_EDGE",EDGE,{"disambiguationData":[OSD([subQ1]),TDD([subQ4])],"isStart":false})])],"isStart":false})})])]}),makeQuery(id+"F47.opExtrude","SWEPT_FACE",FACE,{"disambiguationData":[OSD([subQ0]),TDD([makeQuery(id+"F44.boolean.opBoolean","COPY",EDGE,{"derivedFrom":makeQuery(id+"F44.opExtrude","CAP_EDGE",EDGE,{"disambiguationData":[OSD([subQ0]),TDD([makeQuery(id+"F37.boolean.opBoolean","COPY",EDGE,{"derivedFrom":makeQuery(id+"F37.opExtrude","CAP_EDGE",EDGE,{"disambiguationData":[OSD([subQ0]),TDD([makeQuery(id+"F16.opExtrude","CAP_EDGE",EDGE,{"disambiguationData":[OSD([subQ0])],"isStart":false})])],"isStart":false})})])],"isStart":false})})])]})]});}
            fillet(context, id + "F49", {"entities" : qUnion([Q0]), "radius" : 3 * mm, "tangentPropagation" : true, "allowEdgeOverflow" : false});
        }
    });
